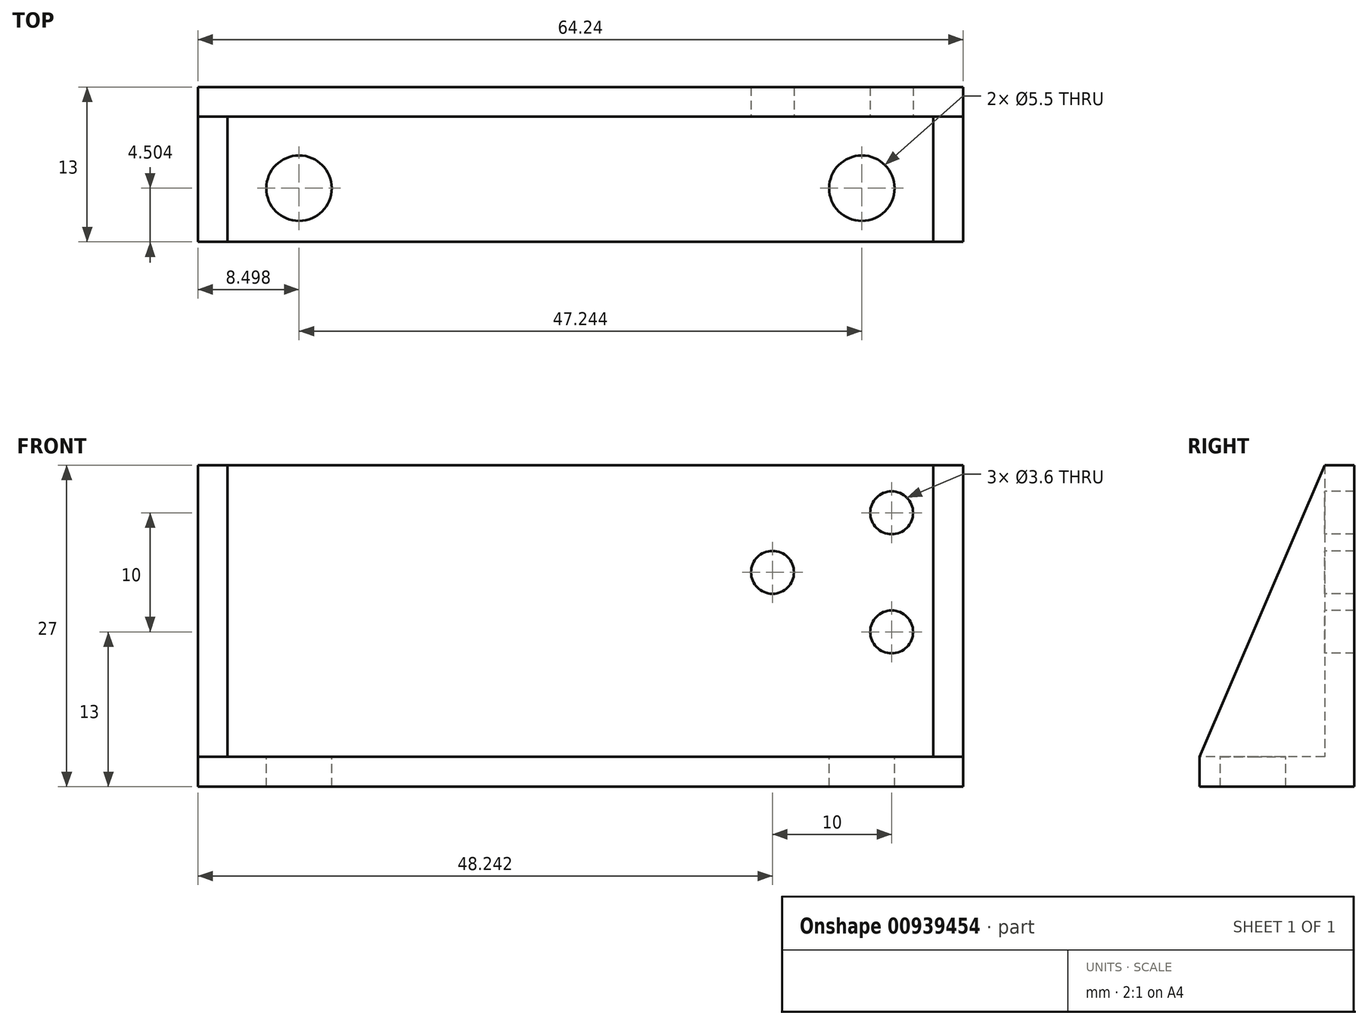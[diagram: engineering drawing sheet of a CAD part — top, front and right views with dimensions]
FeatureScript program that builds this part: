
annotation { "Feature Type Name" : "Feature", "Feature Type Description" : "" }
export const myFeature = defineFeature(function(context is Context, id is Id, definition is map)
    precondition{}
    {
        {
            var Q0;
            Q0=qCreatedBy(makeId("Top.planeOp"),FACE);
            var sketch = newSketch(context, id + "F0", { "sketchPlane" : qUnion([Q0])});
            skLineSegment(sketch, "E0", {"start": v(-25.02, 42.12) * mm, "end": v(-65.02, 42.12) * mm, "construction": true});
            skArc(sketch, "E1", {"start": v(-25.02, 42.12) * mm, "mid": v(-22.14, 45) * mm, "end": v(-25.02, 47.88) * mm, "construction": true});
            skLineSegment(sketch, "E2", {"start": v(-65.02, 47.88) * mm, "end": v(-25.02, 47.88) * mm, "construction": true});
            skArc(sketch, "E3", {"start": v(-65.02, 47.88) * mm, "mid": v(-67.9, 45) * mm, "end": v(-65.02, 42.12) * mm, "construction": true});
            skLineSegment(sketch, "E4", {"start": v(-28.03, 22.8) * mm, "end": v(-28.03, 17.8) * mm});
            skArc(sketch, "E5", {"start": v(-28.03, 22.8) * mm, "mid": v(-29.53, 24.3) * mm, "end": v(-31.03, 22.8) * mm});
            skLineSegment(sketch, "E6", {"start": v(-31.03, 17.8) * mm, "end": v(-31.03, 22.8) * mm});
            skArc(sketch, "E7", {"start": v(-31.03, 17.8) * mm, "mid": v(-29.53, 16.3) * mm, "end": v(-28.03, 17.8) * mm});
            skLineSegment(sketch, "E8", {"start": v(-59.01, 22.8) * mm, "end": v(-59.01, 17.8) * mm});
            skArc(sketch, "E9", {"start": v(-59.01, 22.8) * mm, "mid": v(-60.51, 24.3) * mm, "end": v(-62.01, 22.8) * mm});
            skLineSegment(sketch, "E10", {"start": v(-62.01, 17.8) * mm, "end": v(-62.01, 22.8) * mm});
            skArc(sketch, "E11", {"start": v(-62.01, 17.8) * mm, "mid": v(-60.51, 16.3) * mm, "end": v(-59.01, 17.8) * mm});
            skPoint(sketch, "E12", {"position": v(-68.64, 30.91) * mm});
            skPoint(sketch, "E13", {"position": v(-21.4, 30.91) * mm});
            skLineSegment(sketch, "E14", {"start": v(-68.64, 30.91) * mm, "end": v(-21.4, 30.91) * mm, "construction": true});
            skLineSegment(sketch, "E15.bottom", {"start": v(-12.9, 26.41) * mm, "end": v(-77.14, 26.41) * mm});
            skLineSegment(sketch, "E15.top", {"start": v(-12.9, 39.41) * mm, "end": v(-77.14, 39.41) * mm});
            skLineSegment(sketch, "E15.left", {"start": v(-12.9, 39.41) * mm, "end": v(-12.9, 26.41) * mm});
            skLineSegment(sketch, "E15.right", {"start": v(-77.14, 39.41) * mm, "end": v(-77.14, 26.41) * mm});
            skCircle(sketch, "E16", {"center": v(-21.4, 30.91) * mm, "radius": 2.5 * mm});
            skCircle(sketch, "E17", {"center": v(-68.64, 30.91) * mm, "radius": 2.5 * mm});
            skLineSegment(sketch, "E18", {"start": v(-60.51, 22.8) * mm, "end": v(-29.53, 22.8) * mm});
            skPoint(sketch, "E19", {"position": v(-45.02, 22.8) * mm});
            skPoint(sketch, "E20", {"position": v(-45.02, 26.41) * mm});
            skPoint(sketch, "E21", {"position": v(-45.02, 30.91) * mm});
            skLineSegment(sketch, "E22", {"start": v(-45.02, 30.91) * mm, "end": v(-45.02, 22.8) * mm});
            skSolve(sketch);
        }
        {
            var Q0;
            Q0=makeQuery(id+"F0.imprint","IMPRINT",FACE,{"disambiguationData":[TD([[makeQuery(id+"F0.imprint","IMPRINT",EDGE,{"derivedFrom":sQuery(id+"F0.wireOp",EDGE,"E15.bottom")}),-1.0]])]});
            var Q1;
            Q1=makeQuery(id+"F0.imprint","IMPRINT",FACE,{"disambiguationData":[TD([[makeQuery(id+"F0.imprint","IMPRINT",EDGE,{"derivedFrom":sQuery(id+"F0.wireOp",EDGE,"E17")}),1.0]])]});
            var Q2;
            Q2=makeQuery(id+"F0.imprint","IMPRINT",FACE,{"disambiguationData":[TD([[makeQuery(id+"F0.imprint","IMPRINT",EDGE,{"derivedFrom":sQuery(id+"F0.wireOp",EDGE,"E16")}),1.0]])]});
            extrude(context, id + "F1", {"entities" : qUnion([Q0, Q1, Q2]), "depth" : 27 * mm, "offsetDistance" : 25 * mm});
        }
        {
            var Q0;
            Q0=makeQuery(id+"F1.opExtrude","CAP_FACE",FACE,{"disambiguationData":[OSD([sQuery(id+"F0.wireOp",EDGE,"E15.bottom"),sQuery(id+"F0.wireOp",EDGE,"E15.top"),sQuery(id+"F0.wireOp",EDGE,"E15.left"),sQuery(id+"F0.wireOp",EDGE,"E15.right")])],"isStart":false});
            var Q1;
            Q1=makeQuery(id+"F1.opExtrude","SWEPT_FACE",FACE,{"disambiguationData":[OSD([sQuery(id+"F0.wireOp",EDGE,"E15.bottom")])]});
            shell(context, id + "F2", {"entities" : qUnion([Q0, Q1]), "thickness" : 2.5 * mm});
        }
        {
            var Q0;
            Q0=makeQuery(id+"F2.opShell","OFFSET_FACE",FACE,{"disambiguationData":[OSD([sQuery(id+"F0.wireOp",EDGE,"E15.right")])]});
            var sketch = newSketch(context, id + "F3", { "sketchPlane" : qUnion([Q0])});
            skLineSegment(sketch, "E23", {"start": v(26.41, 2.5) * mm, "end": v(36.91, 27) * mm});
            skLineSegment(sketch, "E24", {"start": v(36.91, 27) * mm, "end": v(26.41, 27) * mm});
            skLineSegment(sketch, "E25", {"start": v(26.41, 27) * mm, "end": v(26.41, 2.5) * mm});
            skSolve(sketch);
        }
        {
            var Q0;
            Q0 = qSketchRegion(id + "F3", true);
            extrude(context, id + "F4", {"entities" : qUnion([Q0]), "operationType" : NewBodyOperationType.REMOVE, "endBound" : BoundingType.THROUGH_ALL, "oppositeDirection" : true, "depth" : 25 * mm, "offsetDistance" : 25 * mm, "hasSecondDirection" : true, "secondDirectionBound" : BoundingType.THROUGH_ALL, "secondDirectionOppositeDirection" : false, "secondDirectionDepth" : 25 * mm});
        }
        {
            var Q0;
            Q0=makeQuery(id+"F1.opExtrude","SWEPT_FACE",FACE,{"disambiguationData":[OSD([sQuery(id+"F0.wireOp",EDGE,"E15.top")])]});
            var sketch = newSketch(context, id + "F5", { "sketchPlane" : qUnion([Q0])});
            skLineSegment(sketch, "E26", {"start": v(18.9, 13) * mm, "end": v(18.9, 23) * mm});
            skLineSegment(sketch, "E27", {"start": v(18.9, 18) * mm, "end": v(28.9, 18) * mm});
            skSolve(sketch);
        }
        {
            var Q0;
            Q0=sQuery(id+"F0.wireOp",VERTEX,"E12");
            var Q1;
            Q1=sQuery(id+"F0.wireOp",VERTEX,"E13");
            var Q2;
            Q2=makeQuery(id+"F1.opExtrude","SWEPT_BODY",BODY,{"disambiguationData":[OSD([sQuery(id+"F0.wireOp",EDGE,"E15.bottom"),sQuery(id+"F0.wireOp",EDGE,"E15.top"),sQuery(id+"F0.wireOp",EDGE,"E15.left"),sQuery(id+"F0.wireOp",EDGE,"E15.right")])]});
            hole(context, id + "F6", {"style" : HoleStyle.SIMPLE, "endStyle" : HoleEndStyle.THROUGH, "oppositeDirection" : true, "standardTappedOrClearance" : lookupTablePath({ "fit" : "Normal", "standard" : "ISO", "size" : "M5", "type" : "Clearance" }), "standardBlindInLast" : lookupTablePath({ "fit" : "Normal", "standard" : "ISO", "engagement" : "75%", "pitch" : "0.8 mm", "size" : "M5", "type" : "Clearance & tapped" }), "holeDiameter" : 5.5 * mm, "majorDiameter" : 5 * mm, "isTappedThrough" : true, "tappedDepth" : 10.5 * mm, "tapClearance" : 3, "startFromSketch" : true, "locations" : qUnion([Q0, Q1]), "scope" : qUnion([Q2])});
        }
        {
            var Q0;
            Q0=sQuery(id+"F5.wireOp",VERTEX,"E26.start");
            var Q1;
            Q1=sQuery(id+"F5.wireOp",VERTEX,"E26.end");
            var Q2;
            Q2=sQuery(id+"F5.wireOp",VERTEX,"E27.end");
            var Q3;
            Q3=makeQuery(id+"F1.opExtrude","SWEPT_BODY",BODY,{"disambiguationData":[OSD([sQuery(id+"F0.wireOp",EDGE,"E15.bottom"),sQuery(id+"F0.wireOp",EDGE,"E15.top"),sQuery(id+"F0.wireOp",EDGE,"E15.left"),sQuery(id+"F0.wireOp",EDGE,"E15.right")])]});
            hole(context, id + "F7", {"style" : HoleStyle.SIMPLE, "endStyle" : HoleEndStyle.THROUGH, "standardTappedOrClearance" : lookupTablePath({ "fit" : "Loose", "standard" : "ISO", "size" : "M3", "type" : "Clearance" }), "standardBlindInLast" : lookupTablePath({ "fit" : "Loose", "standard" : "ISO", "engagement" : "75%", "pitch" : "0.5 mm", "size" : "M3", "type" : "Clearance & tapped" }), "holeDiameter" : 3.6 * mm, "majorDiameter" : 5 * mm, "isTappedThrough" : true, "tappedDepth" : 10.5 * mm, "tapClearance" : 3, "startFromSketch" : true, "locations" : qUnion([Q0, Q1, Q2]), "scope" : qUnion([Q3])});
        }
    });
